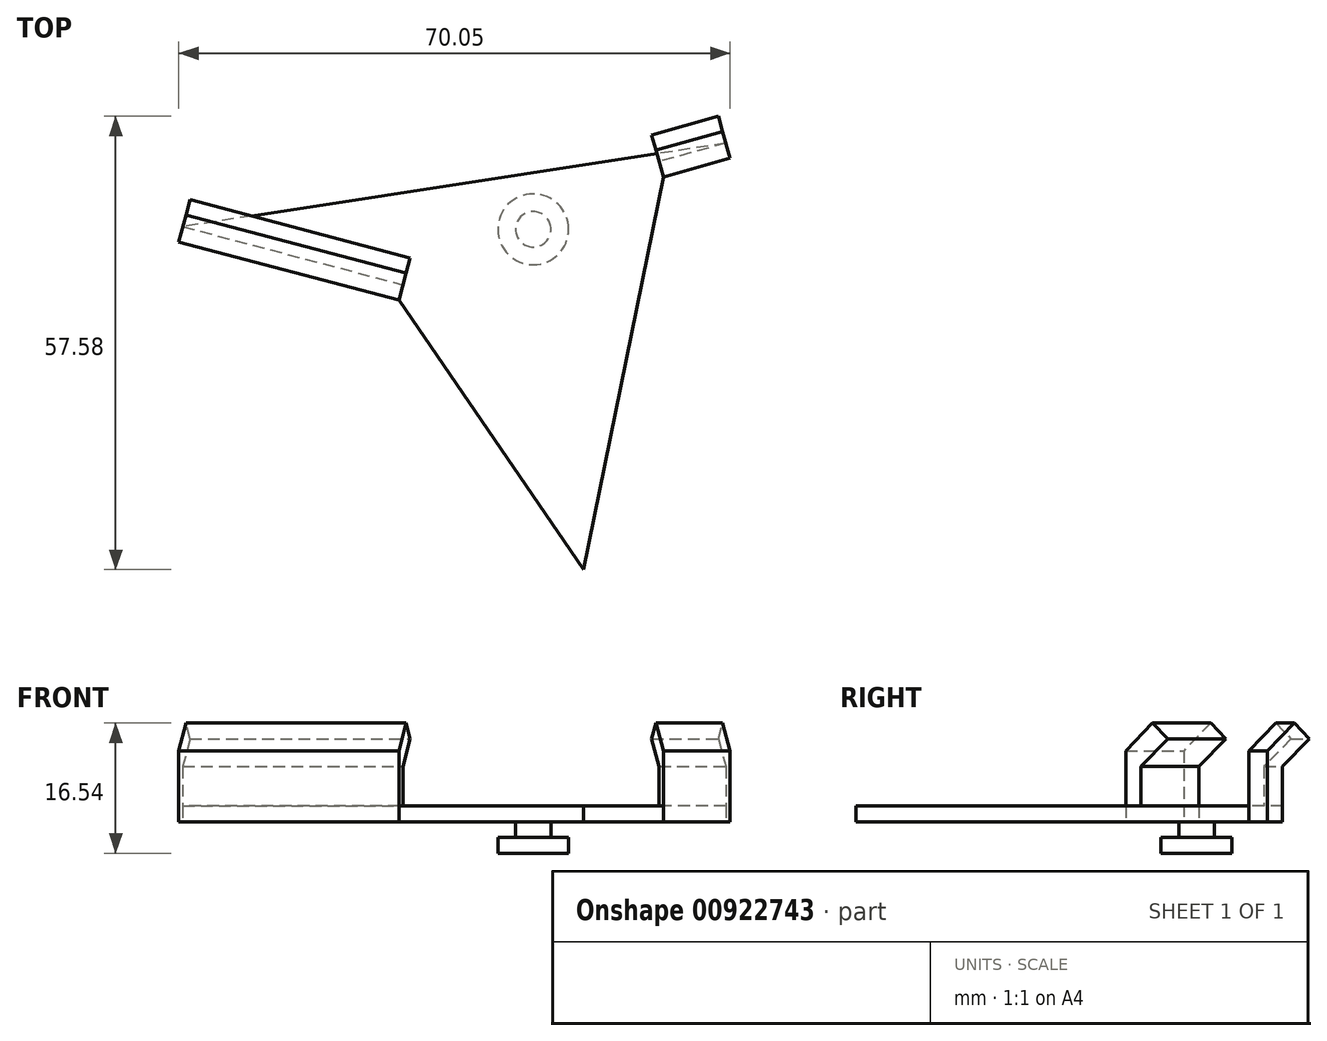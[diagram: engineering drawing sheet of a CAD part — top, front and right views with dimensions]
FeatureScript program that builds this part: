
annotation { "Feature Type Name" : "Feature", "Feature Type Description" : "" }
export const myFeature = defineFeature(function(context is Context, id is Id, definition is map)
    precondition{}
    {
        {
            var Q0;
            Q0=qCreatedBy(makeId("Top.planeOp"),FACE);
            var sketch = newSketch(context, id + "F0", { "sketchPlane" : qUnion([Q0])});
            skLineSegment(sketch, "E0.bottom", {"start": v(0, 0) * mm, "end": v(32.5, 0) * mm, "construction": true});
            skLineSegment(sketch, "E0.top", {"start": v(0, 15.64) * mm, "end": v(32.5, 15.64) * mm, "construction": true});
            skLineSegment(sketch, "E0.left", {"start": v(0, 0) * mm, "end": v(0, 15.64) * mm, "construction": true});
            skLineSegment(sketch, "E0.right", {"start": v(32.5, 0) * mm, "end": v(32.5, 15.64) * mm, "construction": true});
            skLineSegment(sketch, "E1", {"start": v(32.5, 15.64) * mm, "end": v(41, 18) * mm, "construction": true});
            skLineSegment(sketch, "E2", {"start": v(0, 0) * mm, "end": v(-28, 7.4) * mm, "construction": true});
            skLineSegment(sketch, "E3", {"start": v(-28, 7.4) * mm, "end": v(-28, 0) * mm, "construction": true});
            skLineSegment(sketch, "E4", {"start": v(0, 0) * mm, "end": v(-28, 0) * mm, "construction": true});
            skLineSegment(sketch, "E5", {"start": v(41, 18) * mm, "end": v(41, 15.64) * mm, "construction": true});
            skLineSegment(sketch, "E6", {"start": v(32.5, 15.64) * mm, "end": v(41, 15.64) * mm, "construction": true});
            skLineSegment(sketch, "E7.0", {"start": v(-0.51, -1.93) * mm, "end": v(-28.51, 5.46) * mm});
            skLineSegment(sketch, "E8.0", {"start": v(33.04, 13.71) * mm, "end": v(41.54, 16.07) * mm});
            skPoint(sketch, "E9.visualSharp", {"position": v(33.04, 13.71) * mm});
            skLineSegment(sketch, "E10", {"start": v(33.04, 13.71) * mm, "end": v(22.93, -36.17) * mm});
            skLineSegment(sketch, "E11", {"start": v(-0.51, -1.93) * mm, "end": v(22.93, -36.17) * mm});
            skLineSegment(sketch, "E12", {"start": v(41, 18) * mm, "end": v(41.54, 16.07) * mm});
            skLineSegment(sketch, "E13", {"start": v(-28.51, 5.46) * mm, "end": v(-28, 7.4) * mm});
            skLineSegment(sketch, "E14", {"start": v(41, 18) * mm, "end": v(-28, 7.4) * mm});
            skSolve(sketch);
        }
        {
            var Q0;
            Q0 = qSketchRegion(id + "F0", true);
            extrude(context, id + "F1", {"entities" : qUnion([Q0]), "depth" : 2 * mm, "offsetDistance" : 25 * mm});
        }
        {
            var Q0;
            Q0=makeQuery(id+"F1.opExtrude","CAP_FACE",FACE,{"disambiguationData":[OSD([sQuery(id+"F0.wireOp",EDGE,"E7.0"),sQuery(id+"F0.wireOp",EDGE,"E8.0"),sQuery(id+"F0.wireOp",EDGE,"E10"),sQuery(id+"F0.wireOp",EDGE,"E11"),sQuery(id+"F0.wireOp",EDGE,"E12"),sQuery(id+"F0.wireOp",EDGE,"E13"),sQuery(id+"F0.wireOp",EDGE,"E14")])],"isStart":false});
            var sketch = newSketch(context, id + "F2", { "sketchPlane" : qUnion([Q0])});
            skLineSegment(sketch, "E15", {"start": v(-0.51, -1.93) * mm, "end": v(-28.51, 5.46) * mm});
            skLineSegment(sketch, "E16", {"start": v(-28.51, 5.46) * mm, "end": v(-28, 7.4) * mm});
            skLineSegment(sketch, "E17", {"start": v(-28, 7.4) * mm, "end": v(0, 0) * mm});
            skLineSegment(sketch, "E18", {"start": v(0, 0) * mm, "end": v(-0.51, -1.93) * mm});
            skLineSegment(sketch, "E19", {"start": v(41.54, 16.07) * mm, "end": v(33.04, 13.71) * mm});
            skLineSegment(sketch, "E20", {"start": v(41, 18) * mm, "end": v(32.5, 15.64) * mm});
            skLineSegment(sketch, "E21", {"start": v(32.5, 15.64) * mm, "end": v(33.04, 13.71) * mm});
            skSolve(sketch);
        }
        {
            var Q0;
            Q0 = qSketchRegion(id + "F2", true);
            var Q1;
            Q1=makeQuery(id+"F2.imprint","IMPRINT",FACE,{"disambiguationData":[TD([[makeQuery(id+"F2.imprint","IMPRINT",EDGE,{"derivedFrom":sQuery(id+"F2.wireOp",EDGE,"E19")}),1.0]])]});
            extrude(context, id + "F3", {"entities" : qUnion([Q0, Q1]), "operationType" : NewBodyOperationType.ADD, "depth" : 7 * mm, "offsetDistance" : 25 * mm});
        }
        {
            var Q0;
            Q0=makeQuery(id+"F3.opExtrude","CAP_EDGE",EDGE,{"disambiguationData":[OSD([sQuery(id+"F2.wireOp",EDGE,"E17")])],"isStart":false});
            var Q1;
            Q1=makeQuery(id+"F3.opExtrude","CAP_EDGE",EDGE,{"disambiguationData":[OSD([sQuery(id+"F2.wireOp",EDGE,"E20")])],"isStart":false});
            chamfer(context, id + "F4", {"entities" : qUnion([Q0, Q1]), "width" : 2 * mm, "tangentPropagation" : true});
        }
        {
            var Q0;
            Q0=makeQuery(id+"F4.opChamfer","BLEND_FACE",FACE,{"disambiguationData":[OSD([sQuery(id+"F2.wireOp",EDGE,"E17")])]});
            var sketch = newSketch(context, id + "F5", { "sketchPlane" : qUnion([Q0])});
            skLineSegment(sketch, "E22", {"start": v(-0.9, -4.87) * mm, "end": v(-29.38, 0.45) * mm});
            skLineSegment(sketch, "E23", {"start": v(-29.38, 0.45) * mm, "end": v(-29.9, -2.33) * mm});
            skLineSegment(sketch, "E24", {"start": v(-29.9, -2.33) * mm, "end": v(-1.43, -7.65) * mm});
            skLineSegment(sketch, "E25", {"start": v(-1.43, -7.65) * mm, "end": v(-0.9, -4.87) * mm});
            skSolve(sketch);
        }
        {
            var Q0;
            Q0 = qSketchRegion(id + "F5", true);
            extrude(context, id + "F6", {"entities" : qUnion([Q0]), "operationType" : NewBodyOperationType.ADD, "depth" : 5 * mm, "offsetDistance" : 25 * mm});
        }
        {
            var Q0;
            Q0=makeQuery(id+"F4.opChamfer","BLEND_FACE",FACE,{"disambiguationData":[OSD([sQuery(id+"F2.wireOp",EDGE,"E20")])]});
            var sketch = newSketch(context, id + "F7", { "sketchPlane" : qUnion([Q0])});
            skLineSegment(sketch, "E26", {"start": v(34.92, 6.4) * mm, "end": v(43.58, 8.1) * mm});
            skLineSegment(sketch, "E27", {"start": v(43.58, 8.1) * mm, "end": v(44.12, 5.33) * mm});
            skLineSegment(sketch, "E28", {"start": v(44.12, 5.33) * mm, "end": v(35.46, 3.63) * mm});
            skLineSegment(sketch, "E29", {"start": v(35.46, 3.63) * mm, "end": v(34.92, 6.4) * mm});
            skSolve(sketch);
        }
        {
            var Q0;
            Q0 = qSketchRegion(id + "F7", true);
            extrude(context, id + "F8", {"entities" : qUnion([Q0]), "operationType" : NewBodyOperationType.ADD, "depth" : 5 * mm, "offsetDistance" : 25 * mm});
        }
        {
            var Q0;
            Q0=makeQuery(id+"F1.opExtrude","CAP_FACE",FACE,{"disambiguationData":[OSD([sQuery(id+"F0.wireOp",EDGE,"E7.0"),sQuery(id+"F0.wireOp",EDGE,"E8.0"),sQuery(id+"F0.wireOp",EDGE,"E10"),sQuery(id+"F0.wireOp",EDGE,"E11"),sQuery(id+"F0.wireOp",EDGE,"E12"),sQuery(id+"F0.wireOp",EDGE,"E13"),sQuery(id+"F0.wireOp",EDGE,"E14")])],"isStart":true});
            var sketch = newSketch(context, id + "F9", { "sketchPlane" : qUnion([Q0])});
            skLineSegment(sketch, "E30", {"start": v(-0.51, 1.93) * mm, "end": v(0, -13.71) * mm, "construction": true});
            skLineSegment(sketch, "E31", {"start": v(0, -13.71) * mm, "end": v(33.04, -13.71) * mm, "construction": true});
            skLineSegment(sketch, "E32", {"start": v(16.52, -13.71) * mm, "end": v(16.52, -7.05) * mm, "construction": true});
            skCircle(sketch, "E33", {"center": v(16.52, -7.05) * mm, "radius": 2.25 * mm});
            skSolve(sketch);
        }
        {
            var Q0;
            Q0 = qSketchRegion(id + "F9", true);
            extrude(context, id + "F10", {"entities" : qUnion([Q0]), "operationType" : NewBodyOperationType.ADD, "depth" : 2 * mm, "offsetDistance" : 25 * mm});
        }
        {
            var Q0;
            Q0=makeQuery(id+"F10.opExtrude","CAP_FACE",FACE,{"disambiguationData":[OSD([sQuery(id+"F9.wireOp",EDGE,"E33")])],"isStart":false});
            var sketch = newSketch(context, id + "F11", { "sketchPlane" : qUnion([Q0])});
            skCircle(sketch, "E34", {"center": v(16.52, -7.05) * mm, "radius": 4.5 * mm});
            skSolve(sketch);
        }
        {
            var Q0;
            Q0 = qSketchRegion(id + "F11", true);
            extrude(context, id + "F12", {"entities" : qUnion([Q0]), "operationType" : NewBodyOperationType.ADD, "depth" : 2 * mm, "offsetDistance" : 25 * mm});
        }
    });
